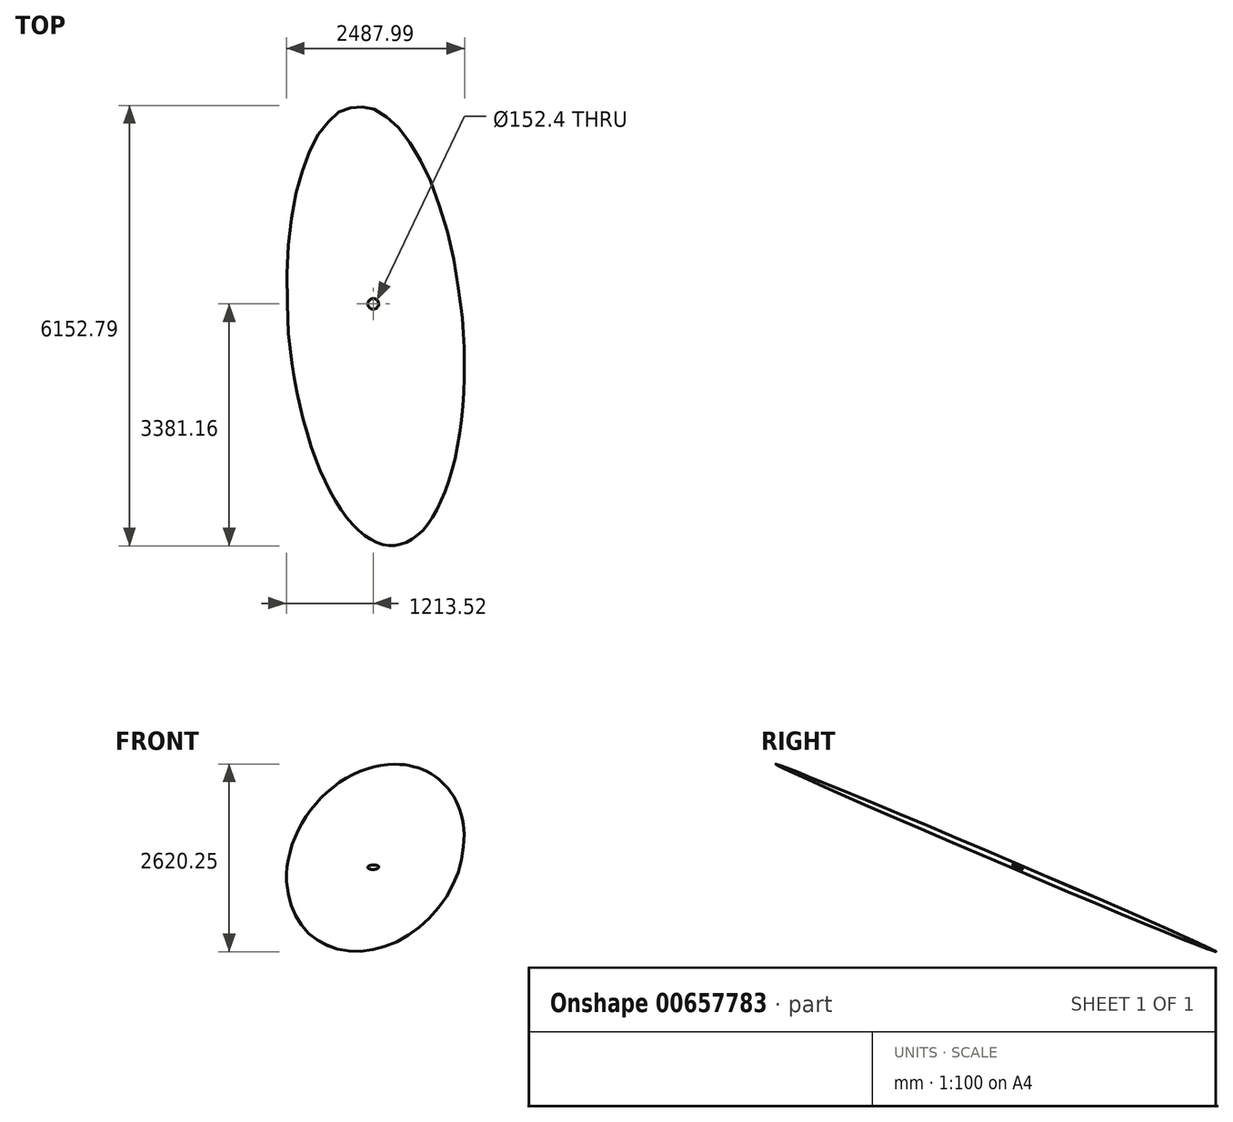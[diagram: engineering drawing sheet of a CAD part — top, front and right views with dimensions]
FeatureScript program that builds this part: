
annotation { "Feature Type Name" : "Feature", "Feature Type Description" : "" }
export const myFeature = defineFeature(function(context is Context, id is Id, definition is map)
    precondition{}
    {
        {
            assignVariable(context, id + "F0", {"name" : "Azimuth", "anyValue" : 265});
        }
        {
            assignVariable(context, id + "F1", {"name" : "Dip", "anyValue" : 23});
        }
        {
            assignVariable(context, id + "F2", {"name" : "Width", "anyValue" : .17});
        }
        {
            var Q0;
            Q0=qCreatedBy(makeId("Top.planeOp"),FACE);
            var sketch = newSketch(context, id + "F3", { "sketchPlane" : qUnion([Q0])});
            skEllipse(sketch, "E0", {"center": v(0, 0) * mm, "majorRadius": 1219.2 * mm, "minorRadius": 3352.8 * mm, "majorAxis": v(0, 1)});
            skLineSegment(sketch, "E1", {"start": v(0, 3124.2) * mm, "end": v(0, -3124.2) * mm, "construction": true});
            skLineSegment(sketch, "E2", {"start": v(-2286, 0) * mm, "end": v(2286, 0) * mm, "construction": true});
            skLineSegment(sketch, "E3.0", {"start": v(30.48, 1219.2) * mm, "end": v(30.48, -1219.2) * mm, "construction": true});
            skLineSegment(sketch, "E4.0", {"start": v(-3352.8, 304.8) * mm, "end": v(3352.8, 304.8) * mm, "construction": true});
            skSolve(sketch);
        }
        {
            var Q0;
            Q0=qCreatedBy(makeId("Top.planeOp"),FACE);
            var sketch = newSketch(context, id + "F4", { "sketchPlane" : qUnion([Q0])});
            skLineSegment(sketch, "E5", {"start": v(0, 0) * mm, "end": v(30.48, 0) * mm});
            skLineSegment(sketch, "E6", {"start": v(30.48, 304.8) * mm, "end": v(30.48, 0) * mm});
            skSolve(sketch);
        }
        {
            var Q0;
            Q0=qSketchRegion(id+"F3",true);
            extrude(context, id + "F5", {"entities" : qUnion([Q0]), "depth" : (getVariable(context, 'Width')) * mm});
        }
        {
            var Q0;
            Q0=qCreatedBy(makeId("Front.planeOp"),FACE);
            var sketch = newSketch(context, id + "F6", { "sketchPlane" : qUnion([Q0])});
            skLineSegment(sketch, "E7", {"start": v(0, 0) * mm, "end": v(0, -4572) * mm, "construction": true});
            skSolve(sketch);
        }
        {
            var Q0;
            Q0=makeQuery(id+"F5.opExtrude","SWEPT_BODY",BODY,{"disambiguationData":[OSD([sQuery(id+"F3.wireOp",EDGE,"E0"),sQuery(id+"F3.wireOp",EDGE,"TMMzbr5i-4nV4-ZnMr-aG6B-IGJ66UyS6uPJ")])]});
            var Q1;
            Q1=sQuery(id+"F3.wireOp",EDGE,"E1");
            transform(context, id + "F7", {"entities" : qUnion([Q0]), "transformType" : TransformType.ROTATION, "transformAxis" : qUnion([Q1]), "angle" : (getVariable(context, 'Dip')) * degree, "oppositeDirection" : true, "makeCopy" : false});
        }
        {
            var Q0;
            Q0=makeQuery(id+"F5.opExtrude","SWEPT_BODY",BODY,{"disambiguationData":[OSD([sQuery(id+"F3.wireOp",EDGE,"E0")])]});
            var Q1;
            Q1=sQuery(id+"F6.wireOp",EDGE,"E7");
            transform(context, id + "F8", {"entities" : qUnion([Q0]), "transformType" : TransformType.ROTATION, "transformAxis" : qUnion([Q1]), "angle" : (getVariable(context, 'Azimuth')) * degree, "makeCopy" : false});
        }
        {
            var Q0;
            Q0=makeQuery(id+"F5.opExtrude","SWEPT_BODY",BODY,{"disambiguationData":[OSD([sQuery(id+"F3.wireOp",EDGE,"E0"),sQuery(id+"F3.wireOp",EDGE,"TMMzbr5i-4nV4-ZnMr-aG6B-IGJ66UyS6uPJ")])]});
            var Q1;
            Q1=sQuery(id+"F4.wireOp",EDGE,"E5");
            transform(context, id + "F9", {"entities" : qUnion([Q0]), "transformType" : TransformType.TRANSLATION_ENTITY, "oppositeDirectionEntity" : false, "transformLine" : qUnion([Q1]), "makeCopy" : false});
        }
        {
            var Q0;
            Q0=makeQuery(id+"F5.opExtrude","SWEPT_BODY",BODY,{"disambiguationData":[OSD([sQuery(id+"F3.wireOp",EDGE,"E0"),sQuery(id+"F3.wireOp",EDGE,"TMMzbr5i-4nV4-ZnMr-aG6B-IGJ66UyS6uPJ")])]});
            var Q1;
            Q1=sQuery(id+"F4.wireOp",EDGE,"E6");
            transform(context, id + "F10", {"entities" : qUnion([Q0]), "transformType" : TransformType.TRANSLATION_ENTITY, "oppositeDirectionEntity" : false, "transformLine" : qUnion([Q1]), "makeCopy" : false});
        }
        {
            var Q0;
            Q0=qCreatedBy(makeId("Top.planeOp"),FACE);
            var sketch = newSketch(context, id + "F11", { "sketchPlane" : qUnion([Q0])});
            skCircle(sketch, "E8", {"center": v(0, 0) * mm, "radius": 76.2 * mm});
            skSolve(sketch);
        }
        {
            var Q0;
            Q0=qSketchRegion(id+"F11",true);
            extrude(context, id + "F12", {"entities" : qUnion([Q0]), "operationType" : NewBodyOperationType.REMOVE, "endBound" : BoundingType.THROUGH_ALL, "oppositeDirection" : true, "depth" : 30.48 * mm, "hasSecondDirection" : true, "secondDirectionBound" : SecondDirectionBoundingType.THROUGH_ALL, "secondDirectionOppositeDirection" : false, "secondDirectionDepth" : 30.48 * mm});
        }
        {
            var Q0;
            Q0=qCreatedBy(makeId("Front.planeOp"),FACE);
            var sketch = newSketch(context, id + "F13", { "sketchPlane" : qUnion([Q0])});
            skLineSegment(sketch, "E9", {"start": v(0, -124.39) * mm, "end": v(0, -4572) * mm});
            skSolve(sketch);
        }
        {
            var Q0;
            Q0=makeQuery(id+"F5.opExtrude","SWEPT_BODY",BODY,{"disambiguationData":[OSD([sQuery(id+"F3.wireOp",EDGE,"E0")])]});
            var Q1;
            Q1=sQuery(id+"F13.wireOp",EDGE,"E9");
            transform(context, id + "F14", {"entities" : qUnion([Q0]), "transformType" : TransformType.TRANSLATION_ENTITY, "oppositeDirectionEntity" : false, "transformLine" : qUnion([Q1]), "makeCopy" : false});
        }
    });
